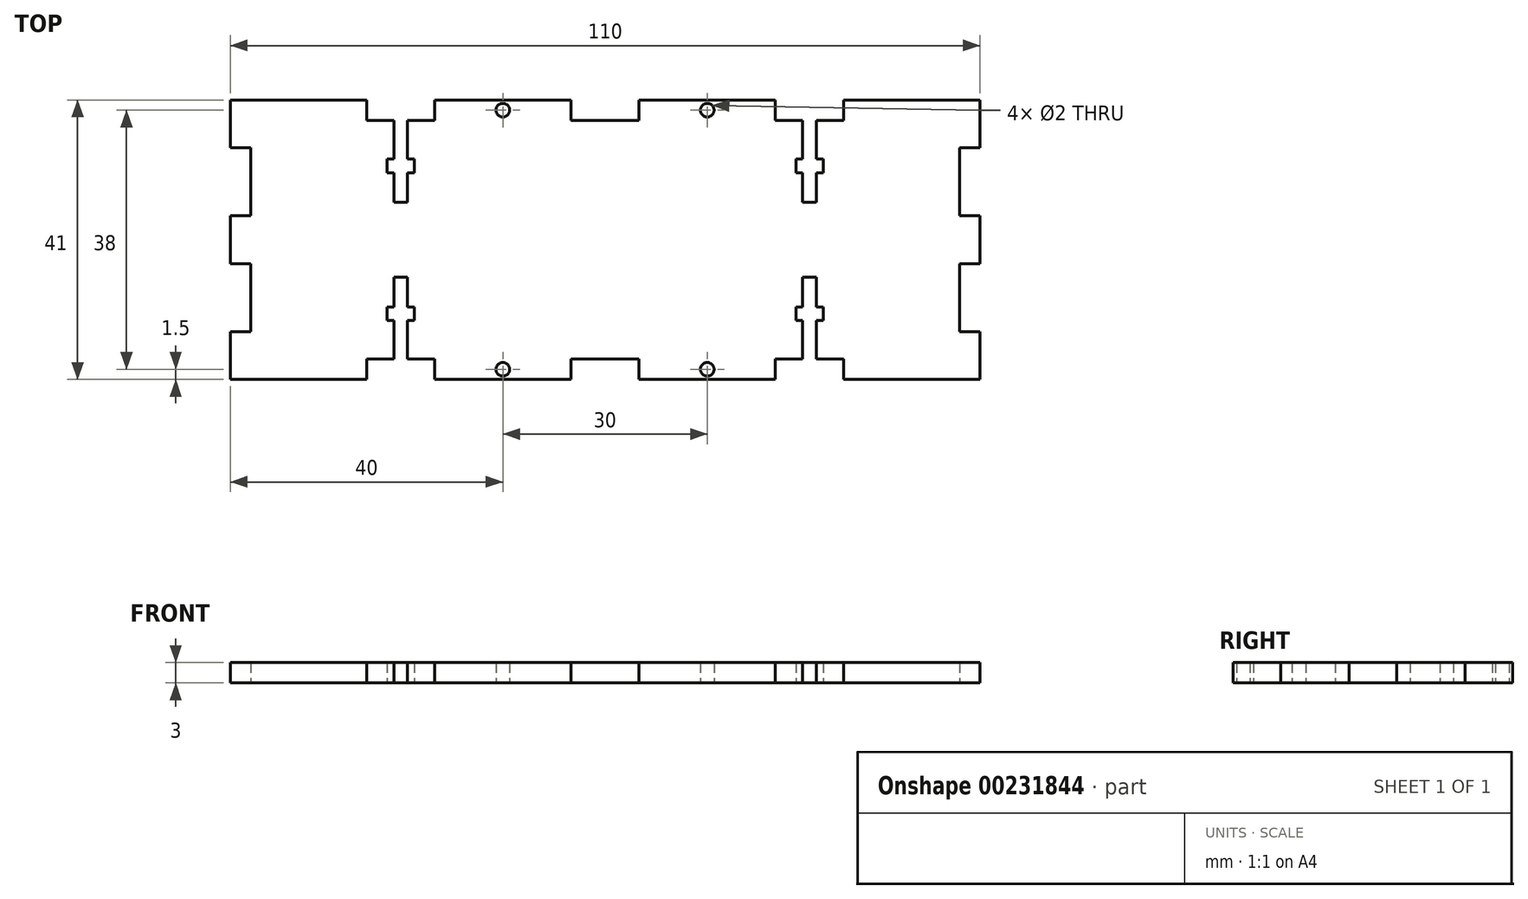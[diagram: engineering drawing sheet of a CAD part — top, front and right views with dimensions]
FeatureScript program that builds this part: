
annotation { "Feature Type Name" : "Feature", "Feature Type Description" : "" }
export const myFeature = defineFeature(function(context is Context, id is Id, definition is map)
    precondition{}
    {
        {
            var Q0;
            Q0=qCreatedBy(makeId("Top.planeOp"),FACE);
            var sketch = newSketch(context, id + "F0", { "sketchPlane" : qUnion([Q0])});
            skLineSegment(sketch, "E0", {"start": v(0, 0) * mm, "end": v(0, 7) * mm});
            skLineSegment(sketch, "E1", {"start": v(0, 7) * mm, "end": v(-3, 7) * mm});
            skLineSegment(sketch, "E2", {"start": v(-3, 7) * mm, "end": v(-3, 17) * mm});
            skLineSegment(sketch, "E3", {"start": v(-3, 17) * mm, "end": v(0, 17) * mm});
            skLineSegment(sketch, "E4", {"start": v(0, 17) * mm, "end": v(0, 24) * mm});
            skLineSegment(sketch, "E5", {"start": v(0, 24) * mm, "end": v(-3, 24) * mm});
            skLineSegment(sketch, "E6", {"start": v(-3, 24) * mm, "end": v(-3, 34) * mm});
            skLineSegment(sketch, "E7", {"start": v(-3, 34) * mm, "end": v(0, 34) * mm});
            skLineSegment(sketch, "E8", {"start": v(0, 34) * mm, "end": v(0, 41) * mm});
            skLineSegment(sketch, "E9", {"start": v(0, 41) * mm, "end": v(-20, 41) * mm});
            skLineSegment(sketch, "E10", {"start": v(-20, 41) * mm, "end": v(-20, 38) * mm});
            skLineSegment(sketch, "E11", {"start": v(-20, 38) * mm, "end": v(-24, 38) * mm});
            skLineSegment(sketch, "E12", {"start": v(-30, 38) * mm, "end": v(-30, 41) * mm});
            skLineSegment(sketch, "E13", {"start": v(-30, 41) * mm, "end": v(-50, 41) * mm});
            skLineSegment(sketch, "E14", {"start": v(-50, 41) * mm, "end": v(-50, 38) * mm});
            skLineSegment(sketch, "E15", {"start": v(-50, 38) * mm, "end": v(-60, 38) * mm});
            skLineSegment(sketch, "E16", {"start": v(-60, 38) * mm, "end": v(-60, 41) * mm});
            skLineSegment(sketch, "E17", {"start": v(-60, 41) * mm, "end": v(-80, 41) * mm});
            skLineSegment(sketch, "E18", {"start": v(-80, 41) * mm, "end": v(-80, 38) * mm});
            skLineSegment(sketch, "E19", {"start": v(-80, 38) * mm, "end": v(-84, 38) * mm});
            skLineSegment(sketch, "E20", {"start": v(-90, 38) * mm, "end": v(-90, 41) * mm});
            skLineSegment(sketch, "E21", {"start": v(-90, 41) * mm, "end": v(-110, 41) * mm});
            skLineSegment(sketch, "E22", {"start": v(-55, 38) * mm, "end": v(-55, -8.75) * mm, "construction": true});
            skLineSegment(sketch, "E23", {"start": v(0, 20.5) * mm, "end": v(-122.84, 20.5) * mm, "construction": true});
            skPoint(sketch, "E23.endSnap0", {"position": v(0, 20.5) * mm});
            skCircle(sketch, "E24", {"center": v(-40, 39.5) * mm, "radius": 1 * mm});
            skPoint(sketch, "E24.centerSnap0", {"position": v(-30, 39.5) * mm});
            skPoint(sketch, "E24.centerSnap1", {"position": v(-40, 41) * mm});
            skCircle(sketch, "E25.MirrorC", {"center": v(-70, 39.5) * mm, "radius": 1 * mm});
            skLineSegment(sketch, "E26.MirrorCS", {"start": v(-110, 7) * mm, "end": v(-107, 7) * mm});
            skLineSegment(sketch, "E27.MirrorCS", {"start": v(-107, 17) * mm, "end": v(-110, 17) * mm});
            skLineSegment(sketch, "E28.MirrorCS", {"start": v(-110, 17) * mm, "end": v(-110, 24) * mm});
            skLineSegment(sketch, "E29.MirrorCS", {"start": v(-107, 34) * mm, "end": v(-110, 34) * mm});
            skLineSegment(sketch, "E30.MirrorCS", {"start": v(-110, 24) * mm, "end": v(-107, 24) * mm});
            skLineSegment(sketch, "E31.MirrorCS", {"start": v(-110, 0) * mm, "end": v(-110, 7) * mm});
            skLineSegment(sketch, "E32.MirrorCS", {"start": v(-107, 7) * mm, "end": v(-107, 17) * mm});
            skPoint(sketch, "E33.MirrorP", {"position": v(-110, 20.5) * mm});
            skLineSegment(sketch, "E34.MirrorCS", {"start": v(-107, 24) * mm, "end": v(-107, 34) * mm});
            skLineSegment(sketch, "E35.MirrorCS", {"start": v(-110, 34) * mm, "end": v(-110, 41) * mm});
            skLineSegment(sketch, "E36.MirrorCS", {"start": v(-60, 3) * mm, "end": v(-60, 0) * mm});
            skLineSegment(sketch, "E37.MirrorCS", {"start": v(-80, 0) * mm, "end": v(-80, 3) * mm});
            skLineSegment(sketch, "E38.MirrorCS", {"start": v(-90, 3) * mm, "end": v(-90, 0) * mm});
            skLineSegment(sketch, "E39.MirrorCS", {"start": v(-107, 7) * mm, "end": v(-110, 7) * mm});
            skLineSegment(sketch, "E40.MirrorCS", {"start": v(-30, 3) * mm, "end": v(-30, 0) * mm});
            skLineSegment(sketch, "E41.MirrorCS", {"start": v(-20, 0) * mm, "end": v(-20, 3) * mm});
            skLineSegment(sketch, "E42.MirrorCS", {"start": v(-3, 7) * mm, "end": v(0, 7) * mm});
            skLineSegment(sketch, "E43.MirrorCS", {"start": v(-50, 0) * mm, "end": v(-50, 3) * mm});
            skLineSegment(sketch, "E44.MirrorCS", {"start": v(-110, 7) * mm, "end": v(-110, 0) * mm});
            skLineSegment(sketch, "E45.MirrorCS", {"start": v(-20, 3) * mm, "end": v(-24, 3) * mm});
            skLineSegment(sketch, "E46.MirrorCS", {"start": v(0, 0) * mm, "end": v(-20, 0) * mm});
            skLineSegment(sketch, "E47.MirrorCS", {"start": v(0, 7) * mm, "end": v(0, 0) * mm});
            skLineSegment(sketch, "E48.MirrorCS", {"start": v(-50, 3) * mm, "end": v(-60, 3) * mm});
            skLineSegment(sketch, "E49.MirrorCS", {"start": v(-60, 0) * mm, "end": v(-80, 0) * mm});
            skLineSegment(sketch, "E50.MirrorCS", {"start": v(-30, 0) * mm, "end": v(-50, 0) * mm});
            skLineSegment(sketch, "E51.MirrorCS", {"start": v(-90, 0) * mm, "end": v(-110, 0) * mm});
            skLineSegment(sketch, "E52.MirrorCS", {"start": v(-80, 3) * mm, "end": v(-84, 3) * mm});
            skCircle(sketch, "E53.MirrorC", {"center": v(-40, 1.5) * mm, "radius": 1 * mm});
            skCircle(sketch, "E54.MirrorC", {"center": v(-70, 1.5) * mm, "radius": 1 * mm});
            skLineSegment(sketch, "E55", {"start": v(-25, 38) * mm, "end": v(-25, 16.35) * mm, "construction": true});
            skPoint(sketch, "E55.endSnap0", {"position": v(-25, 38) * mm});
            skLineSegment(sketch, "E56.top", {"start": v(-26, 26) * mm, "end": v(-24, 26) * mm});
            skLineSegment(sketch, "E56.left", {"start": v(-26, 38) * mm, "end": v(-26, 32.34) * mm});
            skLineSegment(sketch, "E56.right", {"start": v(-24, 38) * mm, "end": v(-24, 32.34) * mm});
            skLineSegment(sketch, "E57.trimOffspring", {"start": v(-26, 38) * mm, "end": v(-30, 38) * mm});
            skLineSegment(sketch, "E58.bottom", {"start": v(-27, 32.34) * mm, "end": v(-26, 32.34) * mm});
            skLineSegment(sketch, "E58.top", {"start": v(-27, 30.34) * mm, "end": v(-26, 30.34) * mm});
            skLineSegment(sketch, "E58.left", {"start": v(-27, 32.34) * mm, "end": v(-27, 30.34) * mm});
            skLineSegment(sketch, "E58.right", {"start": v(-23, 32.34) * mm, "end": v(-23, 30.34) * mm});
            skLineSegment(sketch, "E59.trimOffspring", {"start": v(-24, 32.34) * mm, "end": v(-23, 32.34) * mm});
            skLineSegment(sketch, "E60.trimOffspring", {"start": v(-26, 30.34) * mm, "end": v(-26, 26) * mm});
            skLineSegment(sketch, "E61.trimOffspring", {"start": v(-24, 30.34) * mm, "end": v(-23, 30.34) * mm});
            skLineSegment(sketch, "E62.trimOffspring", {"start": v(-24, 30.34) * mm, "end": v(-24, 26) * mm});
            skLineSegment(sketch, "E63.MirrorCS", {"start": v(-24, 8.66) * mm, "end": v(-23, 8.66) * mm});
            skLineSegment(sketch, "E64.MirrorCS", {"start": v(-24, 10.66) * mm, "end": v(-23, 10.66) * mm});
            skLineSegment(sketch, "E65.MirrorCS", {"start": v(-27, 10.66) * mm, "end": v(-26, 10.66) * mm});
            skLineSegment(sketch, "E66.MirrorCS", {"start": v(-27, 8.66) * mm, "end": v(-26, 8.66) * mm});
            skLineSegment(sketch, "E67.MirrorCS", {"start": v(-24, 3) * mm, "end": v(-24, 8.66) * mm});
            skPoint(sketch, "E68.MirrorP", {"position": v(-25, 3) * mm});
            skLineSegment(sketch, "E69.MirrorCS", {"start": v(-26, 3) * mm, "end": v(-26, 8.66) * mm});
            skLineSegment(sketch, "E70.MirrorCS", {"start": v(-24, 10.66) * mm, "end": v(-24, 15) * mm});
            skLineSegment(sketch, "E71.MirrorCS", {"start": v(-26, 15) * mm, "end": v(-24, 15) * mm});
            skLineSegment(sketch, "E72.MirrorCS", {"start": v(-26, 10.66) * mm, "end": v(-26, 15) * mm});
            skLineSegment(sketch, "E73.MirrorCS", {"start": v(-27, 8.66) * mm, "end": v(-27, 10.66) * mm});
            skLineSegment(sketch, "E74.MirrorCS", {"start": v(-23, 8.66) * mm, "end": v(-23, 10.66) * mm});
            skLineSegment(sketch, "E75.trimOffspring", {"start": v(-26, 3) * mm, "end": v(-30, 3) * mm});
            skLineSegment(sketch, "E76.MirrorCS", {"start": v(-86, 30.34) * mm, "end": v(-87, 30.34) * mm});
            skLineSegment(sketch, "E77.MirrorCS", {"start": v(-84, 15) * mm, "end": v(-86, 15) * mm});
            skLineSegment(sketch, "E78.MirrorCS", {"start": v(-86, 8.66) * mm, "end": v(-87, 8.66) * mm});
            skLineSegment(sketch, "E79.MirrorCS", {"start": v(-86, 32.34) * mm, "end": v(-87, 32.34) * mm});
            skLineSegment(sketch, "E80.MirrorCS", {"start": v(-83, 8.66) * mm, "end": v(-84, 8.66) * mm});
            skLineSegment(sketch, "E81.MirrorCS", {"start": v(-83, 10.66) * mm, "end": v(-84, 10.66) * mm});
            skLineSegment(sketch, "E82.MirrorCS", {"start": v(-87, 32.34) * mm, "end": v(-87, 30.34) * mm});
            skLineSegment(sketch, "E83.MirrorCS", {"start": v(-83, 32.34) * mm, "end": v(-83, 30.34) * mm});
            skLineSegment(sketch, "E84.MirrorCS", {"start": v(-84, 26) * mm, "end": v(-86, 26) * mm});
            skLineSegment(sketch, "E85.MirrorCS", {"start": v(-87, 8.66) * mm, "end": v(-87, 10.66) * mm});
            skLineSegment(sketch, "E86.MirrorCS", {"start": v(-86, 10.66) * mm, "end": v(-87, 10.66) * mm});
            skLineSegment(sketch, "E87.MirrorCS", {"start": v(-83, 8.66) * mm, "end": v(-83, 10.66) * mm});
            skLineSegment(sketch, "E88.MirrorCS", {"start": v(-83, 30.34) * mm, "end": v(-84, 30.34) * mm});
            skLineSegment(sketch, "E89.MirrorCS", {"start": v(-83, 32.34) * mm, "end": v(-84, 32.34) * mm});
            skLineSegment(sketch, "E90.MirrorCS", {"start": v(-86, 30.34) * mm, "end": v(-86, 26) * mm});
            skLineSegment(sketch, "E91.MirrorCS", {"start": v(-86, 10.66) * mm, "end": v(-86, 15) * mm});
            skLineSegment(sketch, "E92.MirrorCS", {"start": v(-86, 38) * mm, "end": v(-86, 32.34) * mm});
            skLineSegment(sketch, "E93.MirrorCS", {"start": v(-84, 3) * mm, "end": v(-84, 8.66) * mm});
            skLineSegment(sketch, "E94.MirrorCS", {"start": v(-84, 38) * mm, "end": v(-84, 32.34) * mm});
            skLineSegment(sketch, "E95.MirrorCS", {"start": v(-84, 30.34) * mm, "end": v(-84, 26) * mm});
            skPoint(sketch, "E96.MirrorP", {"position": v(-85, 3) * mm});
            skLineSegment(sketch, "E97.MirrorCS", {"start": v(-85, 38) * mm, "end": v(-85, 16.35) * mm, "construction": true});
            skLineSegment(sketch, "E98.MirrorCS", {"start": v(-86, 3) * mm, "end": v(-86, 8.66) * mm});
            skLineSegment(sketch, "E99.MirrorCS", {"start": v(-84, 10.66) * mm, "end": v(-84, 15) * mm});
            skPoint(sketch, "E100.MirrorP", {"position": v(-85, 38) * mm});
            skLineSegment(sketch, "E101.trimOffspring", {"start": v(-86, 38) * mm, "end": v(-90, 38) * mm});
            skLineSegment(sketch, "E102.trimOffspring", {"start": v(-86, 3) * mm, "end": v(-90, 3) * mm});
            skSolve(sketch);
        }
        {
            var Q0;
            Q0 = qSketchRegion(id + "F0", true);
            extrude(context, id + "F1", {"entities" : qUnion([Q0]), "depth" : 3 * mm});
        }
    });
